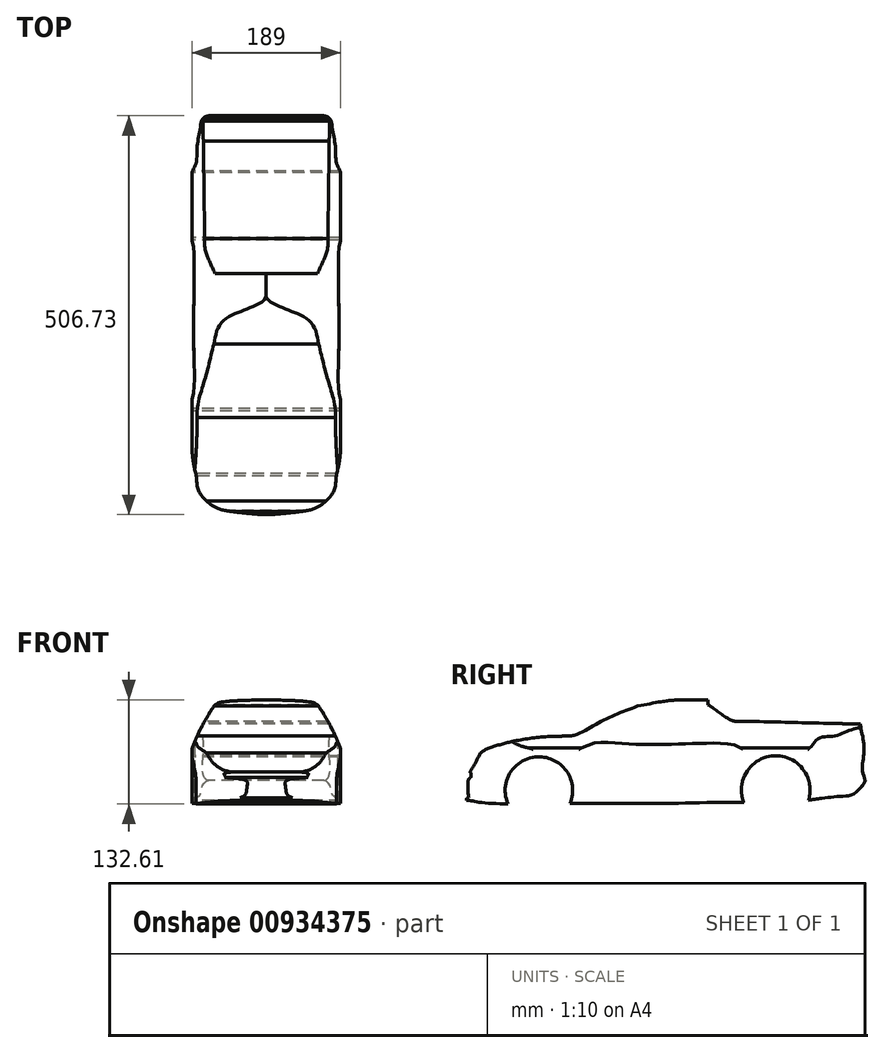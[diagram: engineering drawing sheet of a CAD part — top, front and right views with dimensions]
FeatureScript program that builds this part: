
annotation { "Feature Type Name" : "Feature", "Feature Type Description" : "" }
export const myFeature = defineFeature(function(context is Context, id is Id, definition is map)
    precondition{}
    {
        {
            var Q0;
            Q0=qCreatedBy(makeId("Right.planeOp"),FACE);
            var sketch = newSketch(context, id + "F0", { "sketchPlane" : qUnion([Q0])});
            skLineSegment(sketch, "E0", {"start": v(252, 0) * mm, "end": v(-252, 0) * mm});
            skLineSegment(sketch, "E1", {"start": v(0, 74) * mm, "end": v(0, -74) * mm});
            skSolve(sketch);
        }
        {
            var Q0;
            Q0=qCreatedBy(makeId("Right.planeOp"),FACE);
            var sketch = newSketch(context, id + "F1", { "sketchPlane" : qUnion([Q0])});
            skFitSpline(sketch, "E2", {"points": [v(-240.55, 9.73) * mm, v(-232.56, 14.46) * mm, v(-198.29, 24.5) * mm, v(-161.58, 29.9) * mm, v(-134.6, 30.98) * mm], "startDerivative": vector(47.12, 32.2) * mm, "endDerivative": vector(102.96, 1.88) * mm});
            skFitSpline(sketch, "E3", {"points": [v(-240.55, 9.73) * mm, v(-240.79, 7.68) * mm, v(-239.21, 5.79) * mm, v(-235.3, 4.37) * mm, v(-229.45, 6.8) * mm, v(-221.51, 10.27) * mm, v(-210.28, 13.33) * mm, v(-176.9, 19.24) * mm, v(-146.88, 22.48) * mm, v(-139.26, 24.7) * mm, v(-134.6, 30.98) * mm], "startDerivative": vector(-62.08, -56.9) * mm, "endDerivative": vector(47.71, 82.06) * mm});
            skFitSpline(sketch, "E4", {"points": [v(-253.86, -14.66) * mm, v(-246.17, -8.66) * mm, v(-241.1, -1.64) * mm, v(-239.21, 5.79) * mm], "startDerivative": vector(22.9, 16.04) * mm, "endDerivative": vector(4.1, 24.13) * mm});
            skFitSpline(sketch, "E5", {"points": [v(-253.86, -14.66) * mm, v(-250.15, -8.46) * mm, v(-245.76, -0.9) * mm, v(-242.32, 5.79) * mm, v(-240.55, 9.73) * mm], "startDerivative": vector(14.08, 23.52) * mm, "endDerivative": vector(8.13, 18.63) * mm});
            skFitSpline(sketch, "E6", {"points": [v(-253.86, -14.66) * mm, v(-252.34, -16.89) * mm, v(-252.5, -21.54) * mm, v(-249.33, -23.7) * mm, v(-248.11, -26.13) * mm, v(-248.18, -39.48) * mm, v(-249.53, -44.48) * mm, v(-255.2, -47.24) * mm, v(-257.96, -47.85) * mm], "startDerivative": vector(22.5, -19.29) * mm, "endDerivative": vector(-24.8, -4.15) * mm});
            skFitSpline(sketch, "E7", {"points": [v(-257.96, -47.85) * mm, v(-257.96, -50.35) * mm], "startDerivative": vector(0, -2.5) * mm, "endDerivative": vector(0, -2.5) * mm});
            skFitSpline(sketch, "E8", {"points": [v(-257.96, -50.35) * mm, v(-250, -51.43) * mm, v(-239.21, -53.31) * mm, v(-224.57, -54.53) * mm, v(-205.4, -55.34) * mm], "startDerivative": vector(39.1, -4.6) * mm, "endDerivative": vector(64.58, -2.47) * mm});
            skFitSpline(sketch, "E9", {"points": [v(-255.2, -47.24) * mm, v(-255.84, -44.2) * mm, v(-256.12, -34.13) * mm, v(-256.12, -26.54) * mm, v(-255.2, -23.3) * mm, v(-252.5, -21.54) * mm], "startDerivative": vector(-4.71, 16.23) * mm, "endDerivative": vector(19.64, 9.23) * mm});
            skFitSpline(sketch, "E10", {"points": [v(-126.53, -54.53) * mm, v(-77.43, -54.53) * mm, v(-9.32, -54.53) * mm, v(57.6, -53.31) * mm, v(94.02, -53.31) * mm], "startDerivative": vector(198.55, 2.29) * mm, "endDerivative": vector(164.14, -3.04) * mm});
            skFitSpline(sketch, "E11", {"points": [v(176.4, -50.35) * mm, v(218.6, -45.41) * mm, v(233.46, -42.66) * mm, v(245.88, -30.33) * mm, v(248.77, -25.35) * mm], "startDerivative": vector(117.35, 17.63) * mm, "endDerivative": vector(20.7, 29.34) * mm});
            skFitSpline(sketch, "E12", {"points": [v(248.77, -25.35) * mm, v(247.49, -22.63) * mm, v(245.18, -14.42) * mm, v(244.74, -2.86) * mm, v(246.19, 3.86) * mm, v(246.44, 11.31) * mm, v(246.52, 20.78) * mm, v(245.16, 30.4) * mm, v(243.72, 36.02) * mm, v(242.35, 46.3) * mm], "startDerivative": vector(-25.73, 35.97) * mm, "endDerivative": vector(-9.29, 88.14) * mm});
            skFitSpline(sketch, "E13", {"points": [v(48.71, 70.8) * mm, v(48.71, 77.28) * mm], "startDerivative": vector(0, 6.48) * mm, "endDerivative": vector(0, 6.48) * mm});
            skFitSpline(sketch, "E14", {"points": [v(33.6, 77.28) * mm, v(18.9, 77.28) * mm, v(-3.1, 75.8) * mm, v(-40.88, 69.05) * mm], "startDerivative": vector(-54.56, 0.53) * mm, "endDerivative": vector(-95.06, -19.1) * mm});
            skFitSpline(sketch, "E15", {"points": [v(-134.6, 30.98) * mm, v(-121.44, 32.07) * mm, v(-105.25, 39.5) * mm, v(-77.18, 54.47) * mm, v(-40.88, 69.05) * mm], "startDerivative": vector(71.51, -0.07) * mm, "endDerivative": vector(117.4, 43.34) * mm});
            skFitSpline(sketch, "E16", {"points": [v(-121.44, 32.07) * mm, v(-116.04, 30.98) * mm, v(-105.38, 33.15) * mm, v(-83.66, 45.3) * mm, v(-56.4, 58.39) * mm, v(-40.48, 65.94) * mm, v(-40.88, 69.05) * mm], "startDerivative": vector(47.74, -14.18) * mm, "endDerivative": vector(18.02, 56.11) * mm});
            skArc(sketch, "E17", {"start": v(-126.53, -54.53) * mm, "mid": v(-166.58, 4.71) * mm, "end": v(-205.4, -55.34) * mm});
            skArc(sketch, "E18", {"start": v(176.4, -50.35) * mm, "mid": v(133.13, 5.98) * mm, "end": v(94.02, -53.31) * mm});
            skFitSpline(sketch, "E19", {"points": [v(242.35, 46.3) * mm, v(233.69, 46.3) * mm, v(186.81, 48.27) * mm, v(105.65, 50.43) * mm, v(82.44, 50.02) * mm, v(74.89, 52.85) * mm, v(64.36, 60) * mm, v(53.16, 67.97) * mm, v(48.71, 70.8) * mm], "startDerivative": vector(-87.8, -1.48) * mm, "endDerivative": vector(-61.87, 37.73) * mm});
            skLineSegment(sketch, "E20", {"start": v(92.78, 49.89) * mm, "end": v(242.35, 46.3) * mm});
            skLineSegment(sketch, "E21", {"start": v(33.6, 77.28) * mm, "end": v(48.71, 77.28) * mm});
            skSolve(sketch);
        }
        {
            var Q0;
            {var subQ7=sQuery(id+"F1.wireOp",EDGE,"E4");Q0=makeQuery(id+"F1.imprint","IMPRINT",FACE,{"disambiguationData":[TD([[makeQuery(id+"F1.imprint","IMPRINT",EDGE,{"derivedFrom":subQ7}),-1.0]])]});}
            var Q1;
            {var subQ0=sQuery(id+"F1.wireOp",EDGE,"E16");Q1=makeQuery(id+"F1.imprint","IMPRINT",FACE,{"disambiguationData":[TD([[makeQuery(id+"F1.imprint","IMPRINT",EDGE,{"derivedFrom":subQ0}),1.0]])]});}
            var Q2;
            {var subQ0=sQuery(id+"F1.wireOp",EDGE,"E2");Q2=makeQuery(id+"F1.imprint","IMPRINT",FACE,{"disambiguationData":[TD([[makeQuery(id+"F1.imprint","IMPRINT",EDGE,{"derivedFrom":subQ0}),-1.0]])]});}
            var Q3;
            {var subQ0=sQuery(id+"F1.wireOp",EDGE,"E4");Q3=makeQuery(id+"F1.imprint","IMPRINT",FACE,{"disambiguationData":[TD([[makeQuery(id+"F1.imprint","IMPRINT",EDGE,{"derivedFrom":subQ0}),1.0]])]});}
            var Q4;
            {var subQ0=sQuery(id+"F1.wireOp",EDGE,"E9");Q4=makeQuery(id+"F1.imprint","IMPRINT",FACE,{"disambiguationData":[TD([[makeQuery(id+"F1.imprint","IMPRINT",EDGE,{"derivedFrom":subQ0}),-1.0]])]});}
            extrude(context, id + "F2", {"entities" : qUnion([Q0, Q1, Q2, Q3, Q4]), "endBound" : BoundingType.SYMMETRIC, "depth" : 189 * mm, "offsetDistance" : 25 * mm});
        }
        {
            var Q0;
            Q0=qCreatedBy(makeId("Front.planeOp"),FACE);
            var sketch = newSketch(context, id + "F3", { "sketchPlane" : qUnion([Q0])});
            skFitSpline(sketch, "E22", {"points": [v(-94.07, 15.93) * mm, v(-85.84, 35.46) * mm, v(-77.6, 50.99) * mm, v(-67.01, 68.16) * mm, v(-62.07, 72.63) * mm, v(-48.9, 75.22) * mm, v(0, 77.27) * mm], "startDerivative": vector(47.37, 117.98) * mm, "endDerivative": vector(211.56, 7.2) * mm});
            skFitSpline(sketch, "E23.MirrorCS", {"points": [v(94.07, 15.93) * mm, v(85.84, 35.46) * mm, v(77.6, 50.99) * mm, v(67.01, 68.16) * mm, v(62.07, 72.63) * mm, v(48.9, 75.22) * mm, v(0, 77.27) * mm], "startDerivative": vector(-47.37, 117.98) * mm, "endDerivative": vector(-211.56, 7.2) * mm});
            skLineSegment(sketch, "E24", {"start": v(-94.07, 15.93) * mm, "end": v(-117.5, 15.93) * mm});
            skLineSegment(sketch, "E25", {"start": v(-117.5, 15.93) * mm, "end": v(-117.5, 125.14) * mm});
            skLineSegment(sketch, "E26", {"start": v(-117.5, 125.14) * mm, "end": v(118.95, 125.14) * mm});
            skLineSegment(sketch, "E27", {"start": v(118.95, 125.14) * mm, "end": v(118.95, 15.93) * mm});
            skLineSegment(sketch, "E28", {"start": v(118.95, 15.93) * mm, "end": v(94.07, 15.93) * mm});
            skSolve(sketch);
        }
        {
            var Q0;
            Q0=makeQuery(id+"F3.imprint","IMPRINT",FACE,{"disambiguationData":[TD([[makeQuery(id+"F3.imprint","IMPRINT",EDGE,{"derivedFrom":sQuery(id+"F3.wireOp",EDGE,"E22")}),1.0]])]});
            extrude(context, id + "F4", {"entities" : qUnion([Q0]), "operationType" : NewBodyOperationType.REMOVE, "endBound" : BoundingType.SYMMETRIC, "oppositeDirection" : true, "depth" : 600 * mm, "offsetDistance" : 25 * mm});
        }
        {
            var Q0;
            Q0=qCreatedBy(makeId("Top.planeOp"),FACE);
            var sketch = newSketch(context, id + "F5", { "sketchPlane" : qUnion([Q0])});
            skFitSpline(sketch, "E29", {"points": [v(0, -257.96) * mm, v(22.42, -256.35) * mm, v(43.6, -253.95) * mm, v(64.77, -248.43) * mm, v(84.1, -230.94) * mm, v(88.16, -218.23) * mm, v(89.37, -206) * mm, v(92.67, -191.6) * mm, v(95.14, -120.68) * mm, v(91.74, -97.46) * mm, v(92.34, -32.79) * mm, v(92.34, 80.35) * mm, v(94.99, 95.57) * mm, v(95.95, 159.65) * mm, v(93.63, 178.83) * mm, v(89.33, 188.1) * mm, v(87.68, 210.26) * mm, v(83.7, 233.09) * mm, v(79.74, 246.32) * mm, v(55.59, 248.97) * mm, v(0, 250.29) * mm], "startDerivative": vector(386.84, 3.8) * mm, "endDerivative": vector(-837.36, 34.95) * mm});
            skFitSpline(sketch, "E30.MirrorCS", {"points": [v(0, -257.96) * mm, v(-22.42, -256.35) * mm, v(-43.6, -253.95) * mm, v(-64.77, -248.43) * mm, v(-84.1, -230.94) * mm, v(-88.16, -218.23) * mm, v(-89.37, -206) * mm, v(-92.67, -191.6) * mm, v(-95.14, -120.68) * mm, v(-91.74, -97.46) * mm, v(-92.34, -32.79) * mm, v(-92.34, 80.35) * mm, v(-94.99, 95.57) * mm, v(-95.95, 159.65) * mm, v(-93.63, 178.83) * mm, v(-89.33, 188.1) * mm, v(-87.68, 210.26) * mm, v(-83.7, 233.09) * mm, v(-79.74, 246.32) * mm, v(-55.59, 248.97) * mm, v(0, 250.29) * mm], "startDerivative": vector(-386.84, 3.8) * mm, "endDerivative": vector(837.36, 34.95) * mm});
            skLineSegment(sketch, "E31.bottom", {"start": v(196.23, -337.2) * mm, "end": v(-211.33, -337.2) * mm});
            skLineSegment(sketch, "E31.top", {"start": v(196.23, 337.66) * mm, "end": v(-211.33, 337.66) * mm});
            skLineSegment(sketch, "E31.left", {"start": v(196.23, -337.2) * mm, "end": v(196.23, 337.66) * mm});
            skLineSegment(sketch, "E31.right", {"start": v(-211.33, -337.2) * mm, "end": v(-211.33, 337.66) * mm});
            skLineSegment(sketch, "E32", {"start": v(-55.59, 248.97) * mm, "end": v(55.59, 248.97) * mm});
            skLineSegment(sketch, "E33.top", {"start": v(-55.59, 323.2) * mm, "end": v(55.59, 323.2) * mm});
            skLineSegment(sketch, "E33.left", {"start": v(-55.59, 248.97) * mm, "end": v(-55.59, 323.2) * mm});
            skLineSegment(sketch, "E33.right", {"start": v(55.59, 248.97) * mm, "end": v(55.59, 323.2) * mm});
            skSolve(sketch);
        }
        {
            var Q0;
            {var subQ0=sQuery(id+"F5.wireOp",EDGE,"aCLMEhkP-rxPZ-HwvV-Iok5-T0WrR2dQChRn");Q0=makeQuery(id+"F5.imprint","IMPRINT",FACE,{"disambiguationData":[TD([[makeQuery(id+"F5.imprint","IMPRINT",EDGE,{"derivedFrom":subQ0}),-1.0]])]});}
            var Q1;
            Q1=makeQuery(id+"F5.imprint","IMPRINT",FACE,{"disambiguationData":[TD([[makeQuery(id+"F5.imprint","IMPRINT",EDGE,{"derivedFrom":sQuery(id+"F5.wireOp",EDGE,"E31.bottom")}),-1.0]])]});
            var Q2;
            Q2=makeQuery(id+"F5.imprint","IMPRINT",FACE,{"disambiguationData":[TD([[makeQuery(id+"F5.imprint","IMPRINT",EDGE,{"derivedFrom":sQuery(id+"F5.wireOp",EDGE,"E32")}),1.0]])]});
            extrude(context, id + "F6", {"entities" : qUnion([Q0, Q1, Q2]), "operationType" : NewBodyOperationType.REMOVE, "endBound" : BoundingType.SYMMETRIC, "oppositeDirection" : true, "depth" : 200 * mm, "offsetDistance" : 25 * mm});
        }
        {
            var Q0;
            Q0=makeQuery(id+"F4.boolean.opBoolean","INTERSECT",EDGE,{"derivedFrom":[makeQuery(id+"F2.opExtrude","CAP_FACE",FACE,{"disambiguationData":[OSD([sQuery(id+"F1.wireOp",EDGE,"E2"),sQuery(id+"F1.wireOp",EDGE,"E5"),sQuery(id+"F1.wireOp",EDGE,"E6"),sQuery(id+"F1.wireOp",EDGE,"E7"),sQuery(id+"F1.wireOp",EDGE,"E8"),sQuery(id+"F1.wireOp",EDGE,"E9"),sQuery(id+"F1.wireOp",EDGE,"E10"),sQuery(id+"F1.wireOp",EDGE,"E11"),sQuery(id+"F1.wireOp",EDGE,"E12"),sQuery(id+"F1.wireOp",EDGE,"E13"),sQuery(id+"F1.wireOp",EDGE,"3211fdf4-b305-4564-89c7-c9f115780e8b"),sQuery(id+"F1.wireOp",EDGE,"E14"),sQuery(id+"F1.wireOp",EDGE,"E15"),sQuery(id+"F1.wireOp",EDGE,"E17"),sQuery(id+"F1.wireOp",EDGE,"E18"),sQuery(id+"F1.wireOp",EDGE,"E19"),sQuery(id+"F1.wireOp",EDGE,"E20")])],"isStart":false}),makeQuery(id+"F4.opExtrude","SWEPT_FACE",FACE,{"disambiguationData":[OSD([sQuery(id+"F3.wireOp",EDGE,"E28")])]})]});
            var Q1;
            Q1=makeQuery(id+"F6.boolean.opBoolean","INTERSECT",EDGE,{"disambiguationData":[OD(2.0)],"derivedFrom":[makeQuery(id+"F2.opExtrude","CAP_FACE",FACE,{"disambiguationData":[OSD([sQuery(id+"F1.wireOp",EDGE,"E2"),sQuery(id+"F1.wireOp",EDGE,"E5"),sQuery(id+"F1.wireOp",EDGE,"E6"),sQuery(id+"F1.wireOp",EDGE,"E7"),sQuery(id+"F1.wireOp",EDGE,"E8"),sQuery(id+"F1.wireOp",EDGE,"E9"),sQuery(id+"F1.wireOp",EDGE,"E10"),sQuery(id+"F1.wireOp",EDGE,"E11"),sQuery(id+"F1.wireOp",EDGE,"E12"),sQuery(id+"F1.wireOp",EDGE,"E13"),sQuery(id+"F1.wireOp",EDGE,"3211fdf4-b305-4564-89c7-c9f115780e8b"),sQuery(id+"F1.wireOp",EDGE,"E14"),sQuery(id+"F1.wireOp",EDGE,"E15"),sQuery(id+"F1.wireOp",EDGE,"E17"),sQuery(id+"F1.wireOp",EDGE,"E18"),sQuery(id+"F1.wireOp",EDGE,"E19"),sQuery(id+"F1.wireOp",EDGE,"E20")])],"isStart":false}),makeQuery(id+"F6.opExtrude","SWEPT_FACE",FACE,{"disambiguationData":[OSD([sQuery(id+"F5.wireOp",EDGE,"E29")])]})]});
            var Q2;
            Q2=makeQuery(id+"F6.boolean.opBoolean","INTERSECT",EDGE,{"disambiguationData":[OD(1.0)],"derivedFrom":[makeQuery(id+"F2.opExtrude","CAP_FACE",FACE,{"disambiguationData":[OSD([sQuery(id+"F1.wireOp",EDGE,"E2"),sQuery(id+"F1.wireOp",EDGE,"E5"),sQuery(id+"F1.wireOp",EDGE,"E6"),sQuery(id+"F1.wireOp",EDGE,"E7"),sQuery(id+"F1.wireOp",EDGE,"E8"),sQuery(id+"F1.wireOp",EDGE,"E9"),sQuery(id+"F1.wireOp",EDGE,"E10"),sQuery(id+"F1.wireOp",EDGE,"E11"),sQuery(id+"F1.wireOp",EDGE,"E12"),sQuery(id+"F1.wireOp",EDGE,"E13"),sQuery(id+"F1.wireOp",EDGE,"3211fdf4-b305-4564-89c7-c9f115780e8b"),sQuery(id+"F1.wireOp",EDGE,"E14"),sQuery(id+"F1.wireOp",EDGE,"E15"),sQuery(id+"F1.wireOp",EDGE,"E17"),sQuery(id+"F1.wireOp",EDGE,"E18"),sQuery(id+"F1.wireOp",EDGE,"E19"),sQuery(id+"F1.wireOp",EDGE,"E20")])],"isStart":false}),makeQuery(id+"F6.opExtrude","SWEPT_FACE",FACE,{"disambiguationData":[OSD([sQuery(id+"F5.wireOp",EDGE,"E29")])]})]});
            var Q3;
            Q3=makeQuery(id+"F4.boolean.opBoolean","INTERSECT",EDGE,{"derivedFrom":[makeQuery(id+"F2.opExtrude","CAP_FACE",FACE,{"disambiguationData":[OSD([sQuery(id+"F1.wireOp",EDGE,"E2"),sQuery(id+"F1.wireOp",EDGE,"E5"),sQuery(id+"F1.wireOp",EDGE,"E6"),sQuery(id+"F1.wireOp",EDGE,"E7"),sQuery(id+"F1.wireOp",EDGE,"E8"),sQuery(id+"F1.wireOp",EDGE,"E9"),sQuery(id+"F1.wireOp",EDGE,"E10"),sQuery(id+"F1.wireOp",EDGE,"E11"),sQuery(id+"F1.wireOp",EDGE,"E12"),sQuery(id+"F1.wireOp",EDGE,"E13"),sQuery(id+"F1.wireOp",EDGE,"3211fdf4-b305-4564-89c7-c9f115780e8b"),sQuery(id+"F1.wireOp",EDGE,"E14"),sQuery(id+"F1.wireOp",EDGE,"E15"),sQuery(id+"F1.wireOp",EDGE,"E17"),sQuery(id+"F1.wireOp",EDGE,"E18"),sQuery(id+"F1.wireOp",EDGE,"E19"),sQuery(id+"F1.wireOp",EDGE,"E20")])],"isStart":true}),makeQuery(id+"F4.opExtrude","SWEPT_FACE",FACE,{"disambiguationData":[OSD([sQuery(id+"F3.wireOp",EDGE,"E24")])]})]});
            var Q4;
            Q4=makeQuery(id+"F6.boolean.opBoolean","INTERSECT",EDGE,{"disambiguationData":[OD(1.0)],"derivedFrom":[makeQuery(id+"F2.opExtrude","CAP_FACE",FACE,{"disambiguationData":[OSD([sQuery(id+"F1.wireOp",EDGE,"E2"),sQuery(id+"F1.wireOp",EDGE,"E5"),sQuery(id+"F1.wireOp",EDGE,"E6"),sQuery(id+"F1.wireOp",EDGE,"E7"),sQuery(id+"F1.wireOp",EDGE,"E8"),sQuery(id+"F1.wireOp",EDGE,"E9"),sQuery(id+"F1.wireOp",EDGE,"E10"),sQuery(id+"F1.wireOp",EDGE,"E11"),sQuery(id+"F1.wireOp",EDGE,"E12"),sQuery(id+"F1.wireOp",EDGE,"E13"),sQuery(id+"F1.wireOp",EDGE,"3211fdf4-b305-4564-89c7-c9f115780e8b"),sQuery(id+"F1.wireOp",EDGE,"E14"),sQuery(id+"F1.wireOp",EDGE,"E15"),sQuery(id+"F1.wireOp",EDGE,"E17"),sQuery(id+"F1.wireOp",EDGE,"E18"),sQuery(id+"F1.wireOp",EDGE,"E19"),sQuery(id+"F1.wireOp",EDGE,"E20")])],"isStart":true}),makeQuery(id+"F6.opExtrude","SWEPT_FACE",FACE,{"disambiguationData":[OSD([sQuery(id+"F5.wireOp",EDGE,"E30.MirrorCS")])]})]});
            var Q5;
            Q5=makeQuery(id+"F6.boolean.opBoolean","INTERSECT",EDGE,{"disambiguationData":[OD(2.0)],"derivedFrom":[makeQuery(id+"F2.opExtrude","CAP_FACE",FACE,{"disambiguationData":[OSD([sQuery(id+"F1.wireOp",EDGE,"E2"),sQuery(id+"F1.wireOp",EDGE,"E5"),sQuery(id+"F1.wireOp",EDGE,"E6"),sQuery(id+"F1.wireOp",EDGE,"E7"),sQuery(id+"F1.wireOp",EDGE,"E8"),sQuery(id+"F1.wireOp",EDGE,"E9"),sQuery(id+"F1.wireOp",EDGE,"E10"),sQuery(id+"F1.wireOp",EDGE,"E11"),sQuery(id+"F1.wireOp",EDGE,"E12"),sQuery(id+"F1.wireOp",EDGE,"E13"),sQuery(id+"F1.wireOp",EDGE,"3211fdf4-b305-4564-89c7-c9f115780e8b"),sQuery(id+"F1.wireOp",EDGE,"E14"),sQuery(id+"F1.wireOp",EDGE,"E15"),sQuery(id+"F1.wireOp",EDGE,"E17"),sQuery(id+"F1.wireOp",EDGE,"E18"),sQuery(id+"F1.wireOp",EDGE,"E19"),sQuery(id+"F1.wireOp",EDGE,"E20")])],"isStart":true}),makeQuery(id+"F6.opExtrude","SWEPT_FACE",FACE,{"disambiguationData":[OSD([sQuery(id+"F5.wireOp",EDGE,"E30.MirrorCS")])]})]});
            fillet(context, id + "F7", {"entities" : qUnion([Q0, Q1, Q2, Q3, Q4, Q5]), "radius" : 5 * mm, "tangentPropagation" : true, "allowEdgeOverflow" : false});
        }
    });
